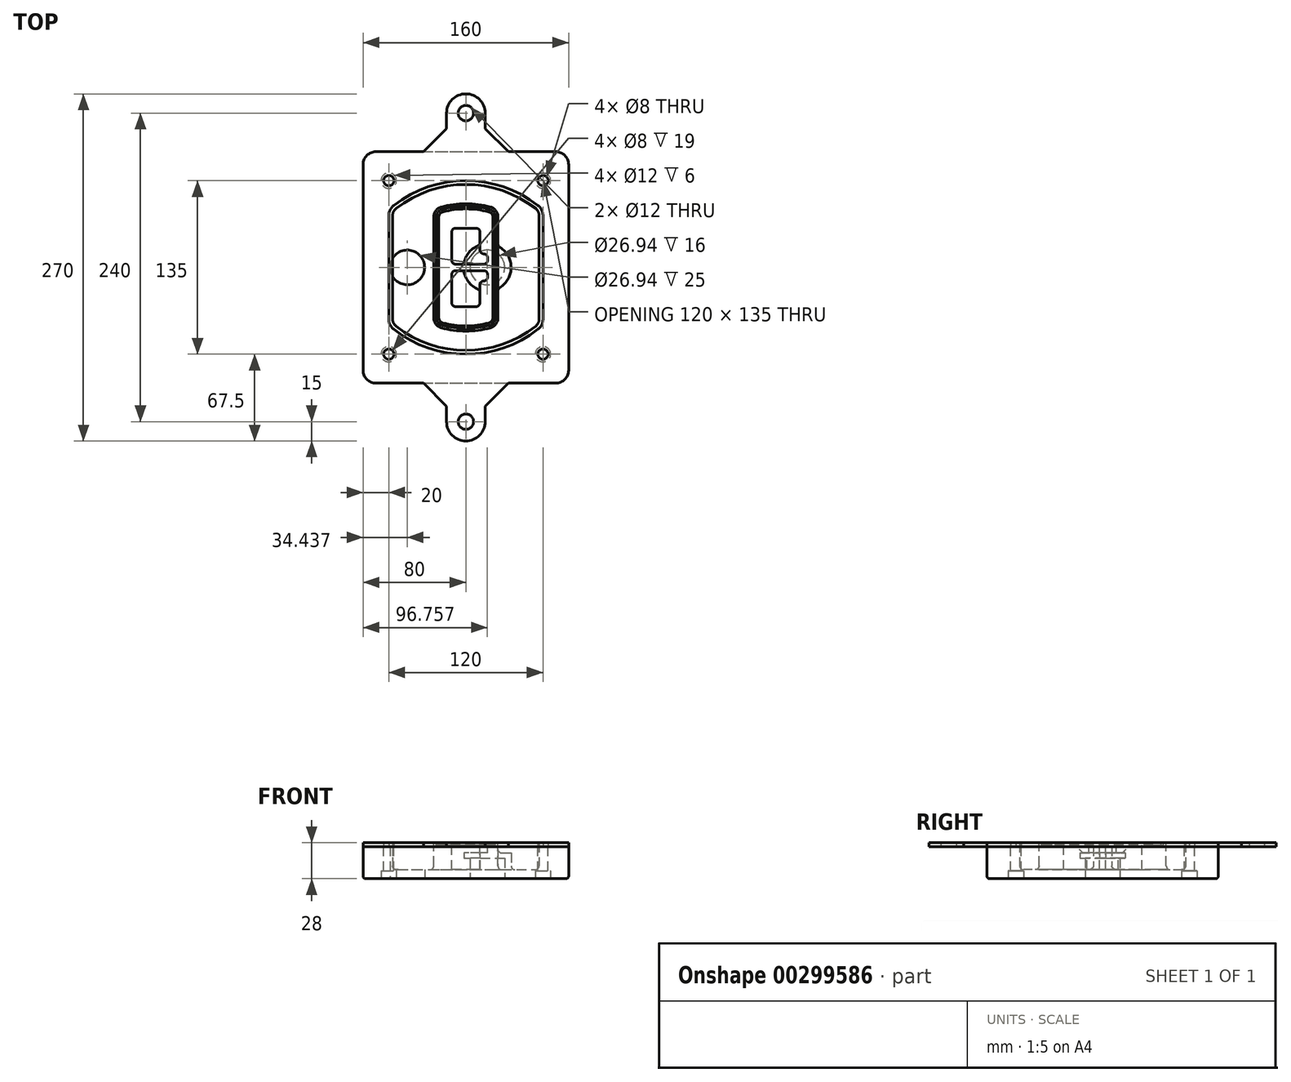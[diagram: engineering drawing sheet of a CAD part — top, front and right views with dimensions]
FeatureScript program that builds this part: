
annotation { "Feature Type Name" : "Feature", "Feature Type Description" : "" }
export const myFeature = defineFeature(function(context is Context, id is Id, definition is map)
    precondition{}
    {
        {
            var Q0;
            Q0=qCreatedBy(makeId("Top.planeOp"),FACE);
            var sketch = newSketch(context, id + "F0", { "sketchPlane" : qUnion([Q0])});
            skPoint(sketch, "E0.rect.middle", {"position": v(0, 0) * mm});
            skLineSegment(sketch, "E1.bottom", {"start": v(-70, -90) * mm, "end": v(70, -90) * mm});
            skLineSegment(sketch, "E1.top", {"start": v(-70, 90) * mm, "end": v(70, 90) * mm});
            skLineSegment(sketch, "E1.left", {"start": v(-80, -80) * mm, "end": v(-80, 80) * mm});
            skLineSegment(sketch, "E1.right", {"start": v(80, -80) * mm, "end": v(80, 80) * mm});
            skLineSegment(sketch, "E2", {"start": v(-80, 90) * mm, "end": v(80, -90) * mm, "construction": true});
            skLineSegment(sketch, "E3", {"start": v(80, 90) * mm, "end": v(-80, -90) * mm, "construction": true});
            skCircle(sketch, "E4", {"center": v(-60, 67.5) * mm, "radius": 4 * mm});
            skCircle(sketch, "E5", {"center": v(60, 67.5) * mm, "radius": 4 * mm});
            skCircle(sketch, "E6", {"center": v(60, -67.5) * mm, "radius": 4 * mm});
            skCircle(sketch, "E7", {"center": v(-60, -67.5) * mm, "radius": 4 * mm});
            skLineSegment(sketch, "E8", {"start": v(-60, 67.5) * mm, "end": v(60, 67.5) * mm, "construction": true});
            skLineSegment(sketch, "E9", {"start": v(60, 67.5) * mm, "end": v(60, -67.5) * mm, "construction": true});
            skLineSegment(sketch, "E10", {"start": v(60, -67.5) * mm, "end": v(-60, -67.5) * mm, "construction": true});
            skLineSegment(sketch, "E11", {"start": v(-60, -67.5) * mm, "end": v(-60, 67.5) * mm, "construction": true});
            skLineSegment(sketch, "E12", {"start": v(-60, 40.3) * mm, "end": v(-60, -40.3) * mm});
            skLineSegment(sketch, "E13", {"start": v(60, 40.3) * mm, "end": v(60, -40.3) * mm});
            skArc(sketch, "E14", {"start": v(56.15, 48.18) * mm, "mid": v(0, 67.5) * mm, "end": v(-56.15, 48.18) * mm});
            skArc(sketch, "E15", {"start": v(-56.15, -48.18) * mm, "mid": v(0, -67.5) * mm, "end": v(56.15, -48.18) * mm});
            skLineSegment(sketch, "E16", {"start": v(-60, 0) * mm, "end": v(60, 0) * mm, "construction": true});
            skPoint(sketch, "E17.visualSharp", {"position": v(-60, -45) * mm});
            skArc(sketch, "E17.filletArc", {"start": v(-60, -40.3) * mm, "mid": v(-58.99, -44.68) * mm, "end": v(-56.15, -48.18) * mm});
            skPoint(sketch, "E18.visualSharp", {"position": v(-60, 45) * mm});
            skArc(sketch, "E18.filletArc", {"start": v(-56.15, 48.18) * mm, "mid": v(-58.99, 44.68) * mm, "end": v(-60, 40.3) * mm});
            skPoint(sketch, "E19.visualSharp", {"position": v(60, 45) * mm});
            skArc(sketch, "E19.filletArc", {"start": v(60, 40.3) * mm, "mid": v(58.99, 44.68) * mm, "end": v(56.15, 48.18) * mm});
            skPoint(sketch, "E20.visualSharp", {"position": v(60, -45) * mm});
            skArc(sketch, "E20.filletArc", {"start": v(56.15, -48.18) * mm, "mid": v(58.99, -44.68) * mm, "end": v(60, -40.3) * mm});
            skPoint(sketch, "E21.visualSharp", {"position": v(-80, 90) * mm});
            skArc(sketch, "E21.filletArc", {"start": v(-70, 90) * mm, "mid": v(-77.07, 87.07) * mm, "end": v(-80, 80) * mm});
            skPoint(sketch, "E22.visualSharp", {"position": v(80, 90) * mm});
            skArc(sketch, "E22.filletArc", {"start": v(80, 80) * mm, "mid": v(77.07, 87.07) * mm, "end": v(70, 90) * mm});
            skPoint(sketch, "E23.visualSharp", {"position": v(80, -90) * mm});
            skArc(sketch, "E23.filletArc", {"start": v(70, -90) * mm, "mid": v(77.07, -87.07) * mm, "end": v(80, -80) * mm});
            skPoint(sketch, "E24.visualSharp", {"position": v(-80, -90) * mm});
            skArc(sketch, "E24.filletArc", {"start": v(-80, -80) * mm, "mid": v(-77.07, -87.07) * mm, "end": v(-70, -90) * mm});
            skArc(sketch, "E25.0", {"start": v(57, 40.3) * mm, "mid": v(56.3, 43.36) * mm, "end": v(54.3, 45.81) * mm});
            skLineSegment(sketch, "E25.1", {"start": v(57, 40.3) * mm, "end": v(57, -40.3) * mm});
            skArc(sketch, "E25.2", {"start": v(54.3, -45.81) * mm, "mid": v(56.3, -43.36) * mm, "end": v(57, -40.3) * mm});
            skArc(sketch, "E25.3", {"start": v(-54.3, -45.81) * mm, "mid": v(0, -64.5) * mm, "end": v(54.3, -45.81) * mm});
            skArc(sketch, "E25.4", {"start": v(-57, -40.3) * mm, "mid": v(-56.3, -43.36) * mm, "end": v(-54.3, -45.81) * mm});
            skArc(sketch, "E25.5", {"start": v(54.3, 45.81) * mm, "mid": v(0, 64.5) * mm, "end": v(-54.3, 45.81) * mm});
            skLineSegment(sketch, "E25.6", {"start": v(-57, 40.3) * mm, "end": v(-57, -40.3) * mm});
            skArc(sketch, "E25.7", {"start": v(-54.3, 45.81) * mm, "mid": v(-56.3, 43.36) * mm, "end": v(-57, 40.3) * mm});
            skArc(sketch, "E26.0", {"start": v(-58.62, 51.33) * mm, "mid": v(-62.58, 46.43) * mm, "end": v(-64, 40.3) * mm});
            skArc(sketch, "E26.1", {"start": v(58.62, 51.33) * mm, "mid": v(0, 71.5) * mm, "end": v(-58.62, 51.33) * mm});
            skArc(sketch, "E26.2", {"start": v(64, 40.3) * mm, "mid": v(62.58, 46.43) * mm, "end": v(58.62, 51.33) * mm});
            skLineSegment(sketch, "E26.3", {"start": v(64, 40.3) * mm, "end": v(64, -40.3) * mm});
            skArc(sketch, "E26.4", {"start": v(58.62, -51.33) * mm, "mid": v(62.58, -46.43) * mm, "end": v(64, -40.3) * mm});
            skLineSegment(sketch, "E26.5", {"start": v(-64, 40.3) * mm, "end": v(-64, -40.3) * mm});
            skArc(sketch, "E26.6", {"start": v(-58.62, -51.33) * mm, "mid": v(0, -71.5) * mm, "end": v(58.62, -51.33) * mm});
            skArc(sketch, "E26.7", {"start": v(-64, -40.3) * mm, "mid": v(-62.58, -46.43) * mm, "end": v(-58.62, -51.33) * mm});
            skSolve(sketch);
        }
        {
            var Q0;
            Q0=makeQuery(id+"F0.imprint","IMPRINT",FACE,{"disambiguationData":[TD([[makeQuery(id+"F0.imprint","IMPRINT",EDGE,{"derivedFrom":sQuery(id+"F0.wireOp",EDGE,"E1.bottom")}),1.0]])]});
            var Q1;
            Q1=makeQuery(id+"F0.imprint","IMPRINT",FACE,{"disambiguationData":[TD([[makeQuery(id+"F0.imprint","IMPRINT",EDGE,{"derivedFrom":sQuery(id+"F0.wireOp",EDGE,"E12")}),1.0]])]});
            var Q2;
            Q2=makeQuery(id+"F0.imprint","IMPRINT",FACE,{"disambiguationData":[TD([[makeQuery(id+"F0.imprint","IMPRINT",EDGE,{"derivedFrom":sQuery(id+"F0.wireOp",EDGE,"E25.0")}),1.0]])]});
            var Q3;
            Q3=makeQuery(id+"F0.imprint","IMPRINT",FACE,{"disambiguationData":[TD([[makeQuery(id+"F0.imprint","IMPRINT",EDGE,{"derivedFrom":sQuery(id+"F0.wireOp",EDGE,"E12")}),-1.0]])]});
            extrude(context, id + "F1", {"entities" : qUnion([Q0, Q1, Q2, Q3]), "oppositeDirection" : true, "depth" : 25 * mm});
        }
        {
            var Q0;
            Q0=makeQuery(id+"F0.imprint","IMPRINT",FACE,{"disambiguationData":[TD([[makeQuery(id+"F0.imprint","IMPRINT",EDGE,{"derivedFrom":sQuery(id+"F0.wireOp",EDGE,"E12")}),1.0]])]});
            extrude(context, id + "F2", {"entities" : qUnion([Q0]), "operationType" : NewBodyOperationType.ADD, "depth" : 3 * mm});
        }
        {
            var Q0;
            Q0=makeQuery(id+"F0.imprint","IMPRINT",FACE,{"disambiguationData":[TD([[makeQuery(id+"F0.imprint","IMPRINT",EDGE,{"derivedFrom":sQuery(id+"F0.wireOp",EDGE,"E25.0")}),1.0]])]});
            extrude(context, id + "F3", {"entities" : qUnion([Q0]), "operationType" : NewBodyOperationType.REMOVE, "oppositeDirection" : true, "depth" : 18 * mm});
        }
        {
            var Q0;
            Q0=makeQuery(id+"F2.opExtrude","CAP_FACE",FACE,{"disambiguationData":[OSD([sQuery(id+"F0.wireOp",EDGE,"E12"),sQuery(id+"F0.wireOp",EDGE,"E13"),sQuery(id+"F0.wireOp",EDGE,"E14"),sQuery(id+"F0.wireOp",EDGE,"E15"),sQuery(id+"F0.wireOp",EDGE,"E17.filletArc"),sQuery(id+"F0.wireOp",EDGE,"E18.filletArc"),sQuery(id+"F0.wireOp",EDGE,"E19.filletArc"),sQuery(id+"F0.wireOp",EDGE,"E20.filletArc"),sQuery(id+"F0.wireOp",EDGE,"E25.0"),sQuery(id+"F0.wireOp",EDGE,"E25.1"),sQuery(id+"F0.wireOp",EDGE,"E25.2"),sQuery(id+"F0.wireOp",EDGE,"E25.3"),sQuery(id+"F0.wireOp",EDGE,"E25.4"),sQuery(id+"F0.wireOp",EDGE,"E25.5"),sQuery(id+"F0.wireOp",EDGE,"E25.6"),sQuery(id+"F0.wireOp",EDGE,"E25.7")])],"isStart":false});
            var sketch = newSketch(context, id + "F4", { "sketchPlane" : qUnion([Q0])});
            skArc(sketch, "E27.0", {"start": v(-19.08, -46.97) * mm, "mid": v(0, -49.5) * mm, "end": v(19.08, -46.97) * mm});
            skArc(sketch, "E28.0", {"start": v(19.08, 46.97) * mm, "mid": v(0, 49.5) * mm, "end": v(-19.08, 46.97) * mm});
            skLineSegment(sketch, "E29", {"start": v(-25, 39.25) * mm, "end": v(-25, -39.25) * mm});
            skLineSegment(sketch, "E30", {"start": v(25, 39.25) * mm, "end": v(25, -39.25) * mm});
            skLineSegment(sketch, "E31", {"start": v(-25, 45.1) * mm, "end": v(25, 45.1) * mm, "construction": true});
            skLineSegment(sketch, "E32", {"start": v(-25, -45.1) * mm, "end": v(25, -45.1) * mm, "construction": true});
            skPoint(sketch, "E33.visualSharp", {"position": v(-25, 45.1) * mm});
            skArc(sketch, "E33.filletArc", {"start": v(-19.08, 46.97) * mm, "mid": v(-23.35, 44.11) * mm, "end": v(-25, 39.25) * mm});
            skPoint(sketch, "E34.visualSharp", {"position": v(25, 45.1) * mm});
            skArc(sketch, "E34.filletArc", {"start": v(25, 39.25) * mm, "mid": v(23.35, 44.11) * mm, "end": v(19.08, 46.97) * mm});
            skPoint(sketch, "E35.visualSharp", {"position": v(25, -45.1) * mm});
            skArc(sketch, "E35.filletArc", {"start": v(19.08, -46.97) * mm, "mid": v(23.35, -44.11) * mm, "end": v(25, -39.25) * mm});
            skPoint(sketch, "E36.visualSharp", {"position": v(-25, -45.1) * mm});
            skArc(sketch, "E36.filletArc", {"start": v(-25, -39.25) * mm, "mid": v(-23.35, -44.11) * mm, "end": v(-19.08, -46.97) * mm});
            skArc(sketch, "E37.0", {"start": v(54.3, 45.81) * mm, "mid": v(0, 64.5) * mm, "end": v(-54.3, 45.81) * mm});
            skArc(sketch, "E37.1", {"start": v(-54.3, 45.81) * mm, "mid": v(-56.3, 43.36) * mm, "end": v(-57, 40.3) * mm});
            skLineSegment(sketch, "E37.2", {"start": v(-57, 40.3) * mm, "end": v(-57, -40.3) * mm});
            skArc(sketch, "E37.3", {"start": v(-57, -40.3) * mm, "mid": v(-56.3, -43.36) * mm, "end": v(-54.3, -45.81) * mm});
            skArc(sketch, "E37.4", {"start": v(-54.3, -45.81) * mm, "mid": v(0, -64.5) * mm, "end": v(54.3, -45.81) * mm});
            skArc(sketch, "E37.5", {"start": v(54.3, -45.81) * mm, "mid": v(56.3, -43.36) * mm, "end": v(57, -40.3) * mm});
            skLineSegment(sketch, "E37.6", {"start": v(57, 40.3) * mm, "end": v(57, -40.3) * mm});
            skArc(sketch, "E37.7", {"start": v(57, 40.3) * mm, "mid": v(56.3, 43.36) * mm, "end": v(54.3, 45.81) * mm});
            skLineSegment(sketch, "E38.0", {"start": v(23, 39.25) * mm, "end": v(23, -39.25) * mm});
            skArc(sketch, "E38.1", {"start": v(18.56, -45.04) * mm, "mid": v(21.76, -42.9) * mm, "end": v(23, -39.25) * mm});
            skArc(sketch, "E38.2", {"start": v(-18.56, -45.04) * mm, "mid": v(0, -47.5) * mm, "end": v(18.56, -45.04) * mm});
            skArc(sketch, "E38.3", {"start": v(-23, -39.25) * mm, "mid": v(-21.76, -42.9) * mm, "end": v(-18.56, -45.04) * mm});
            skLineSegment(sketch, "E38.4", {"start": v(-23, 39.25) * mm, "end": v(-23, -39.25) * mm});
            skArc(sketch, "E38.5", {"start": v(23, 39.25) * mm, "mid": v(21.76, 42.9) * mm, "end": v(18.56, 45.04) * mm});
            skArc(sketch, "E38.6", {"start": v(-18.56, 45.04) * mm, "mid": v(-21.76, 42.9) * mm, "end": v(-23, 39.25) * mm});
            skArc(sketch, "E38.7", {"start": v(18.56, 45.04) * mm, "mid": v(0, 47.5) * mm, "end": v(-18.56, 45.04) * mm});
            skArc(sketch, "E39.0", {"start": v(21, 39.25) * mm, "mid": v(20.18, 41.68) * mm, "end": v(18.04, 43.1) * mm});
            skLineSegment(sketch, "E39.1", {"start": v(21, 39.25) * mm, "end": v(21, -39.25) * mm});
            skArc(sketch, "E39.2", {"start": v(18.04, -43.1) * mm, "mid": v(20.18, -41.68) * mm, "end": v(21, -39.25) * mm});
            skArc(sketch, "E39.3", {"start": v(-18.04, -43.1) * mm, "mid": v(0, -45.5) * mm, "end": v(18.04, -43.1) * mm});
            skArc(sketch, "E39.4", {"start": v(-21, -39.25) * mm, "mid": v(-20.18, -41.68) * mm, "end": v(-18.04, -43.1) * mm});
            skArc(sketch, "E39.5", {"start": v(18.04, 43.1) * mm, "mid": v(0, 45.5) * mm, "end": v(-18.04, 43.1) * mm});
            skLineSegment(sketch, "E39.6", {"start": v(-21, 39.25) * mm, "end": v(-21, -39.25) * mm});
            skArc(sketch, "E39.7", {"start": v(-18.04, 43.1) * mm, "mid": v(-20.18, 41.68) * mm, "end": v(-21, 39.25) * mm});
            skLineSegment(sketch, "E40", {"start": v(-25, 0) * mm, "end": v(25, 0) * mm, "construction": true});
            skLineSegment(sketch, "E41", {"start": v(-11, 5.5) * mm, "end": v(-11, 27.5) * mm});
            skLineSegment(sketch, "E42", {"start": v(-8, 30.5) * mm, "end": v(8, 30.5) * mm});
            skLineSegment(sketch, "E43", {"start": v(11, 27.5) * mm, "end": v(11, 13.5) * mm});
            skLineSegment(sketch, "E44", {"start": v(14, 10.5) * mm, "end": v(14, 10.5) * mm});
            skLineSegment(sketch, "E45", {"start": v(17, 7.5) * mm, "end": v(17, 5.5) * mm});
            skLineSegment(sketch, "E46", {"start": v(14, 2.5) * mm, "end": v(-8, 2.5) * mm});
            skPoint(sketch, "E47.visualSharp", {"position": v(-11, 30.5) * mm});
            skArc(sketch, "E47.filletArc", {"start": v(-8, 30.5) * mm, "mid": v(-10.12, 29.62) * mm, "end": v(-11, 27.5) * mm});
            skPoint(sketch, "E48.visualSharp", {"position": v(11, 30.5) * mm});
            skArc(sketch, "E48.filletArc", {"start": v(11, 27.5) * mm, "mid": v(10.12, 29.62) * mm, "end": v(8, 30.5) * mm});
            skPoint(sketch, "E49.visualSharp", {"position": v(11, 10.5) * mm});
            skArc(sketch, "E49.filletArc", {"start": v(11, 13.5) * mm, "mid": v(11.88, 11.38) * mm, "end": v(14, 10.5) * mm});
            skPoint(sketch, "E50.visualSharp", {"position": v(17, 10.5) * mm});
            skArc(sketch, "E50.filletArc", {"start": v(17, 7.5) * mm, "mid": v(16.12, 9.62) * mm, "end": v(14, 10.5) * mm});
            skPoint(sketch, "E51.visualSharp", {"position": v(17, 2.5) * mm});
            skArc(sketch, "E51.filletArc", {"start": v(14, 2.5) * mm, "mid": v(16.12, 3.38) * mm, "end": v(17, 5.5) * mm});
            skPoint(sketch, "E52.visualSharp", {"position": v(-11, 2.5) * mm});
            skArc(sketch, "E52.filletArc", {"start": v(-11, 5.5) * mm, "mid": v(-10.12, 3.38) * mm, "end": v(-8, 2.5) * mm});
            skLineSegment(sketch, "E53.0.MirrorCS", {"start": v(14, -2.5) * mm, "end": v(-8, -2.5) * mm});
            skArc(sketch, "E54.0.MirrorCS", {"start": v(-11, -5.5) * mm, "mid": v(-10.12, -3.38) * mm, "end": v(-8, -2.5) * mm});
            skLineSegment(sketch, "E55.0.MirrorCS", {"start": v(-11, -5.5) * mm, "end": v(-11, -27.5) * mm});
            skArc(sketch, "E56.0.MirrorCS", {"start": v(-8, -30.5) * mm, "mid": v(-10.12, -29.62) * mm, "end": v(-11, -27.5) * mm});
            skLineSegment(sketch, "E57.0.MirrorCS", {"start": v(-8, -30.5) * mm, "end": v(8, -30.5) * mm});
            skArc(sketch, "E58.0.MirrorCS", {"start": v(11, -27.5) * mm, "mid": v(10.12, -29.62) * mm, "end": v(8, -30.5) * mm});
            skLineSegment(sketch, "E59.0.MirrorCS", {"start": v(11, -27.5) * mm, "end": v(11, -13.5) * mm});
            skArc(sketch, "E60.0.MirrorCS", {"start": v(11, -13.5) * mm, "mid": v(11.88, -11.38) * mm, "end": v(14, -10.5) * mm});
            skArc(sketch, "E61.0.MirrorCS", {"start": v(17, -7.5) * mm, "mid": v(16.12, -9.62) * mm, "end": v(14, -10.5) * mm});
            skLineSegment(sketch, "E62.0.MirrorCS", {"start": v(17, -7.5) * mm, "end": v(17, -5.5) * mm});
            skArc(sketch, "E63.0.MirrorCS", {"start": v(14, -2.5) * mm, "mid": v(16.12, -3.38) * mm, "end": v(17, -5.5) * mm});
            skSolve(sketch);
        }
        {
            var Q0;
            Q0=makeQuery(id+"F4.imprint","IMPRINT",FACE,{"disambiguationData":[TD([[makeQuery(id+"F4.imprint","IMPRINT",EDGE,{"derivedFrom":sQuery(id+"F4.wireOp",EDGE,"E27.0")}),1.0]])]});
            var Q1;
            Q1=makeQuery(id+"F4.imprint","IMPRINT",FACE,{"disambiguationData":[TD([[makeQuery(id+"F4.imprint","IMPRINT",EDGE,{"derivedFrom":sQuery(id+"F4.wireOp",EDGE,"E38.0")}),-1.0]])]});
            var Q2;
            Q2=makeQuery(id+"F4.imprint","IMPRINT",FACE,{"disambiguationData":[TD([[makeQuery(id+"F4.imprint","IMPRINT",EDGE,{"derivedFrom":sQuery(id+"F4.wireOp",EDGE,"E39.0")}),1.0]])]});
            extrude(context, id + "F5", {"entities" : qUnion([Q0, Q1, Q2]), "operationType" : NewBodyOperationType.ADD, "endBound" : BoundingType.UP_TO_NEXT, "oppositeDirection" : true, "depth" : 25 * mm});
        }
        {
            var Q0;
            Q0=makeQuery(id+"F4.imprint","IMPRINT",FACE,{"disambiguationData":[TD([[makeQuery(id+"F4.imprint","IMPRINT",EDGE,{"derivedFrom":sQuery(id+"F4.wireOp",EDGE,"E38.0")}),-1.0]])]});
            extrude(context, id + "F6", {"entities" : qUnion([Q0]), "operationType" : NewBodyOperationType.REMOVE, "oppositeDirection" : true, "depth" : 2 * mm});
        }
        {
            var Q0;
            Q0=makeQuery(id+"F1.opExtrude","CAP_FACE",FACE,{"disambiguationData":[OSD([sQuery(id+"F0.wireOp",EDGE,"E1.bottom"),sQuery(id+"F0.wireOp",EDGE,"E1.top"),sQuery(id+"F0.wireOp",EDGE,"E1.left"),sQuery(id+"F0.wireOp",EDGE,"E1.right"),sQuery(id+"F0.wireOp",EDGE,"E4"),sQuery(id+"F0.wireOp",EDGE,"E5"),sQuery(id+"F0.wireOp",EDGE,"E6"),sQuery(id+"F0.wireOp",EDGE,"E7"),sQuery(id+"F0.wireOp",EDGE,"E21.filletArc"),sQuery(id+"F0.wireOp",EDGE,"E22.filletArc"),sQuery(id+"F0.wireOp",EDGE,"E23.filletArc"),sQuery(id+"F0.wireOp",EDGE,"E24.filletArc")])],"isStart":false});
            var sketch = newSketch(context, id + "F7", { "sketchPlane" : qUnion([Q0])});
            skCircle(sketch, "E64", {"center": v(16.76, 0) * mm, "radius": 13.47 * mm});
            skCircle(sketch, "E65", {"center": v(-45.56, 0) * mm, "radius": 13.47 * mm});
            skLineSegment(sketch, "E66", {"start": v(80, 0) * mm, "end": v(-80, 0) * mm});
            skCircle(sketch, "E67", {"center": v(16.76, 0) * mm, "radius": 18.47 * mm});
            skCircle(sketch, "E68", {"center": v(60, -67.5) * mm, "radius": 6 * mm});
            skCircle(sketch, "E69", {"center": v(-60, -67.5) * mm, "radius": 6 * mm});
            skCircle(sketch, "E70", {"center": v(-60, 67.5) * mm, "radius": 6 * mm});
            skCircle(sketch, "E71", {"center": v(60, 67.5) * mm, "radius": 6 * mm});
            skSolve(sketch);
        }
        {
            var Q0;
            {var subQ1=sQuery(id+"F7.wireOp",EDGE,"E66");var subQ4=sQuery(id+"F7.wireOp",EDGE,"E64");var subQ6=makeQuery(id+"F7.imprint","INTERSECT",VERTEX,{"disambiguationData":[OD(0.0)],"derivedFrom":[subQ4,subQ1]});Q0=makeQuery(id+"F7.imprint","IMPRINT",FACE,{"disambiguationData":[TD([[makeQuery(id+"F7.imprint","IMPRINT",EDGE,{"disambiguationData":[TD([[subQ6,-1.0]])],"derivedFrom":subQ4}),-1.0]])]});}
            var Q1;
            {var subQ0=sQuery(id+"F7.wireOp",EDGE,"E66");var subQ1=sQuery(id+"F7.wireOp",EDGE,"E64");var subQ3=makeQuery(id+"F7.imprint","INTERSECT",VERTEX,{"disambiguationData":[OD(0.0)],"derivedFrom":[subQ1,subQ0]});Q1=makeQuery(id+"F7.imprint","IMPRINT",FACE,{"disambiguationData":[TD([[makeQuery(id+"F7.imprint","IMPRINT",EDGE,{"disambiguationData":[TD([[subQ3,-1.0]])],"derivedFrom":subQ1}),1.0]])]});}
            var Q2;
            {var subQ0=sQuery(id+"F7.wireOp",EDGE,"E66");var subQ1=sQuery(id+"F7.wireOp",EDGE,"E64");var subQ3=makeQuery(id+"F7.imprint","INTERSECT",VERTEX,{"disambiguationData":[OD(0.0)],"derivedFrom":[subQ1,subQ0]});Q2=makeQuery(id+"F7.imprint","IMPRINT",FACE,{"disambiguationData":[TD([[makeQuery(id+"F7.imprint","IMPRINT",EDGE,{"disambiguationData":[TD([[subQ3,1.0]])],"derivedFrom":subQ1}),1.0]])]});}
            var Q3;
            {var subQ1=sQuery(id+"F7.wireOp",EDGE,"E66");var subQ4=sQuery(id+"F7.wireOp",EDGE,"E64");var subQ6=makeQuery(id+"F7.imprint","INTERSECT",VERTEX,{"disambiguationData":[OD(0.0)],"derivedFrom":[subQ4,subQ1]});Q3=makeQuery(id+"F7.imprint","IMPRINT",FACE,{"disambiguationData":[TD([[makeQuery(id+"F7.imprint","IMPRINT",EDGE,{"disambiguationData":[TD([[subQ6,1.0]])],"derivedFrom":subQ4}),-1.0]])]});}
            extrude(context, id + "F8", {"entities" : qUnion([Q0, Q1, Q2, Q3]), "operationType" : NewBodyOperationType.ADD, "oppositeDirection" : true, "depth" : 20 * mm});
        }
        {
            var Q0;
            {var subQ0=sQuery(id+"F7.wireOp",EDGE,"E66");var subQ1=sQuery(id+"F7.wireOp",EDGE,"E64");var subQ3=makeQuery(id+"F7.imprint","INTERSECT",VERTEX,{"disambiguationData":[OD(0.0)],"derivedFrom":[subQ1,subQ0]});Q0=makeQuery(id+"F7.imprint","IMPRINT",FACE,{"disambiguationData":[TD([[makeQuery(id+"F7.imprint","IMPRINT",EDGE,{"disambiguationData":[TD([[subQ3,-1.0]])],"derivedFrom":subQ1}),1.0]])]});}
            var Q1;
            {var subQ0=sQuery(id+"F7.wireOp",EDGE,"E66");var subQ1=sQuery(id+"F7.wireOp",EDGE,"E64");var subQ3=makeQuery(id+"F7.imprint","INTERSECT",VERTEX,{"disambiguationData":[OD(0.0)],"derivedFrom":[subQ1,subQ0]});Q1=makeQuery(id+"F7.imprint","IMPRINT",FACE,{"disambiguationData":[TD([[makeQuery(id+"F7.imprint","IMPRINT",EDGE,{"disambiguationData":[TD([[subQ3,1.0]])],"derivedFrom":subQ1}),1.0]])]});}
            extrude(context, id + "F9", {"entities" : qUnion([Q0, Q1]), "operationType" : NewBodyOperationType.REMOVE, "oppositeDirection" : true, "depth" : 16 * mm});
        }
        {
            var Q0;
            {var subQ0=sQuery(id+"F7.wireOp",EDGE,"E66");var subQ1=sQuery(id+"F7.wireOp",EDGE,"E65");var subQ3=makeQuery(id+"F7.imprint","INTERSECT",VERTEX,{"disambiguationData":[OD(0.0)],"derivedFrom":[subQ1,subQ0]});Q0=makeQuery(id+"F7.imprint","IMPRINT",FACE,{"disambiguationData":[TD([[makeQuery(id+"F7.imprint","IMPRINT",EDGE,{"disambiguationData":[TD([[subQ3,-1.0]])],"derivedFrom":subQ1}),1.0]])]});}
            var Q1;
            {var subQ0=sQuery(id+"F7.wireOp",EDGE,"E66");var subQ1=sQuery(id+"F7.wireOp",EDGE,"E65");var subQ3=makeQuery(id+"F7.imprint","INTERSECT",VERTEX,{"disambiguationData":[OD(0.0)],"derivedFrom":[subQ1,subQ0]});Q1=makeQuery(id+"F7.imprint","IMPRINT",FACE,{"disambiguationData":[TD([[makeQuery(id+"F7.imprint","IMPRINT",EDGE,{"disambiguationData":[TD([[subQ3,1.0]])],"derivedFrom":subQ1}),1.0]])]});}
            extrude(context, id + "F10", {"entities" : qUnion([Q0, Q1]), "operationType" : NewBodyOperationType.REMOVE, "oppositeDirection" : true, "depth" : 25 * mm});
        }
        {
            var Q0;
            Q0=makeQuery(id+"F7.imprint","IMPRINT",FACE,{"disambiguationData":[TD([[makeQuery(id+"F7.imprint","IMPRINT",EDGE,{"derivedFrom":sQuery(id+"F7.wireOp",EDGE,"E68")}),1.0]])]});
            var Q1;
            Q1=makeQuery(id+"F7.imprint","IMPRINT",FACE,{"disambiguationData":[TD([[makeQuery(id+"F7.imprint","IMPRINT",EDGE,{"derivedFrom":makeQuery(id+"F1.opExtrude","CAP_EDGE",EDGE,{"disambiguationData":[OSD([sQuery(id+"F0.wireOp",EDGE,"E5")])],"isStart":false})}),-1.0]])]});
            var Q2;
            Q2=makeQuery(id+"F7.imprint","IMPRINT",FACE,{"disambiguationData":[TD([[makeQuery(id+"F7.imprint","IMPRINT",EDGE,{"derivedFrom":sQuery(id+"F7.wireOp",EDGE,"E69")}),1.0]])]});
            var Q3;
            Q3=makeQuery(id+"F7.imprint","IMPRINT",FACE,{"disambiguationData":[TD([[makeQuery(id+"F7.imprint","IMPRINT",EDGE,{"derivedFrom":makeQuery(id+"F1.opExtrude","CAP_EDGE",EDGE,{"disambiguationData":[OSD([sQuery(id+"F0.wireOp",EDGE,"E4")])],"isStart":false})}),-1.0]])]});
            var Q4;
            Q4=makeQuery(id+"F7.imprint","IMPRINT",FACE,{"disambiguationData":[TD([[makeQuery(id+"F7.imprint","IMPRINT",EDGE,{"derivedFrom":sQuery(id+"F7.wireOp",EDGE,"E70")}),1.0]])]});
            var Q5;
            Q5=makeQuery(id+"F7.imprint","IMPRINT",FACE,{"disambiguationData":[TD([[makeQuery(id+"F7.imprint","IMPRINT",EDGE,{"derivedFrom":makeQuery(id+"F1.opExtrude","CAP_EDGE",EDGE,{"disambiguationData":[OSD([sQuery(id+"F0.wireOp",EDGE,"E7")])],"isStart":false})}),-1.0]])]});
            var Q6;
            Q6=makeQuery(id+"F7.imprint","IMPRINT",FACE,{"disambiguationData":[TD([[makeQuery(id+"F7.imprint","IMPRINT",EDGE,{"derivedFrom":sQuery(id+"F7.wireOp",EDGE,"E71")}),1.0]])]});
            var Q7;
            Q7=makeQuery(id+"F7.imprint","IMPRINT",FACE,{"disambiguationData":[TD([[makeQuery(id+"F7.imprint","IMPRINT",EDGE,{"derivedFrom":makeQuery(id+"F1.opExtrude","CAP_EDGE",EDGE,{"disambiguationData":[OSD([sQuery(id+"F0.wireOp",EDGE,"E6")])],"isStart":false})}),-1.0]])]});
            extrude(context, id + "F11", {"entities" : qUnion([Q0, Q1, Q2, Q3, Q4, Q5, Q6, Q7]), "operationType" : NewBodyOperationType.REMOVE, "oppositeDirection" : true, "depth" : 6 * mm});
        }
        {
            var Q0;
            Q0=makeQuery(id+"F9.boolean.opBoolean","COPY",FACE,{"derivedFrom":makeQuery(id+"F9.opExtrude","CAP_FACE",FACE,{"disambiguationData":[OSD([sQuery(id+"F7.wireOp",EDGE,"E64")])],"isStart":false})});
            var sketch = newSketch(context, id + "F12", { "sketchPlane" : qUnion([Q0])});
            skArc(sketch, "E72.0", {"start": v(11, 17.55) * mm, "mid": v(2.57, 11.82) * mm, "end": v(-1.54, 2.5) * mm});
            skArc(sketch, "E72.1", {"start": v(-1.54, -2.5) * mm, "mid": v(2.57, -11.82) * mm, "end": v(11, -17.55) * mm});
            skLineSegment(sketch, "E73", {"start": v(-1.54, -2.5) * mm, "end": v(14, -2.5) * mm});
            skLineSegment(sketch, "E74.0", {"start": v(14, 2.5) * mm, "end": v(-1.54, 2.5) * mm});
            skArc(sketch, "E74.1", {"start": v(14, 2.5) * mm, "mid": v(16.12, 3.38) * mm, "end": v(17, 5.5) * mm});
            skLineSegment(sketch, "E74.2", {"start": v(17, 7.5) * mm, "end": v(17, 5.5) * mm});
            skArc(sketch, "E74.3", {"start": v(17, 7.5) * mm, "mid": v(16.12, 9.62) * mm, "end": v(14, 10.5) * mm});
            skArc(sketch, "E74.4", {"start": v(11, 13.5) * mm, "mid": v(11.88, 11.38) * mm, "end": v(14, 10.5) * mm});
            skLineSegment(sketch, "E74.5", {"start": v(11, 17.55) * mm, "end": v(11, 13.5) * mm});
            skLineSegment(sketch, "E74.7", {"start": v(14, -2.5) * mm, "end": v(-1.54, -2.5) * mm});
            skArc(sketch, "E74.8", {"start": v(14, -2.5) * mm, "mid": v(16.12, -3.38) * mm, "end": v(17, -5.5) * mm});
            skLineSegment(sketch, "E74.9", {"start": v(17, -7.5) * mm, "end": v(17, -5.5) * mm});
            skArc(sketch, "E74.10", {"start": v(17, -7.5) * mm, "mid": v(16.12, -9.62) * mm, "end": v(14, -10.5) * mm});
            skArc(sketch, "E74.11", {"start": v(11, -13.5) * mm, "mid": v(11.88, -11.38) * mm, "end": v(14, -10.5) * mm});
            skLineSegment(sketch, "E74.12", {"start": v(11, -17.55) * mm, "end": v(11, -13.5) * mm});
            skPoint(sketch, "E75.orphan", {"position": v(11, -27.5) * mm});
            skPoint(sketch, "E76.orphan", {"position": v(-8, -2.5) * mm});
            skPoint(sketch, "E77.orphan", {"position": v(-8, 2.5) * mm});
            skPoint(sketch, "E78.orphan", {"position": v(11, 27.5) * mm});
            skSolve(sketch);
        }
        {
            var Q0;
            {var subQ7=sQuery(id+"F12.wireOp",EDGE,"E72.0");var subQ14=sQuery(id+"F12.wireOp",EDGE,"E72.1");var subQ16=sQuery(id+"F12.wireOp",EDGE,"E74.1");var subQ18=sQuery(id+"F12.wireOp",EDGE,"E74.8");Q0=qUnion([makeQuery(id+"F12.imprint","IMPRINT",FACE,{"disambiguationData":[TD([[makeQuery(id+"F12.imprint","IMPRINT",EDGE,{"derivedFrom":subQ7}),1.0]])]}),makeQuery(id+"F12.imprint","IMPRINT",FACE,{"disambiguationData":[TD([[makeQuery(id+"F12.imprint","IMPRINT",EDGE,{"derivedFrom":subQ14}),1.0]])]}),makeQuery(id+"F12.imprint","IMPRINT",FACE,{"disambiguationData":[TD([[makeQuery(id+"F12.imprint","IMPRINT",EDGE,{"derivedFrom":subQ16}),1.0]])]}),makeQuery(id+"F12.imprint","IMPRINT",FACE,{"disambiguationData":[TD([[makeQuery(id+"F12.imprint","IMPRINT",EDGE,{"derivedFrom":subQ18}),-1.0]])]})]);}
            var Q1;
            Q1=makeQuery(id+"F5.boolean.opBoolean","SPLIT",FACE,{"disambiguationData":[TD([makeQuery(id+"F5.opExtrude","SWEPT_FACE",FACE,{"disambiguationData":[OSD([sQuery(id+"F4.wireOp",EDGE,"E41")])]})])],"derivedFrom":makeQuery(id+"F3.boolean.opBoolean","COPY",FACE,{"derivedFrom":makeQuery(id+"F3.opExtrude","CAP_FACE",FACE,{"disambiguationData":[OSD([sQuery(id+"F0.wireOp",EDGE,"E25.0"),sQuery(id+"F0.wireOp",EDGE,"E25.1"),sQuery(id+"F0.wireOp",EDGE,"E25.2"),sQuery(id+"F0.wireOp",EDGE,"E25.3"),sQuery(id+"F0.wireOp",EDGE,"E25.4"),sQuery(id+"F0.wireOp",EDGE,"E25.5"),sQuery(id+"F0.wireOp",EDGE,"E25.6"),sQuery(id+"F0.wireOp",EDGE,"E25.7")])],"isStart":false})})});
            extrude(context, id + "F13", {"entities" : qUnion([Q0]), "operationType" : NewBodyOperationType.REMOVE, "endBound" : BoundingType.UP_TO_SURFACE, "endBoundEntityFace" : qUnion([Q1]), "depth" : 25 * mm});
        }
        {
            var Q0;
            Q0=makeQuery(id+"F3.boolean.opBoolean","COPY",EDGE,{"derivedFrom":makeQuery(id+"F3.opExtrude","CAP_EDGE",EDGE,{"disambiguationData":[OSD([sQuery(id+"F0.wireOp",EDGE,"E25.6")])],"isStart":false})});
            var Q1;
            Q1=makeQuery(id+"F8.boolean.opBoolean","INTERSECT",EDGE,{"derivedFrom":[makeQuery(id+"F5.opExtrude","SWEPT_FACE",FACE,{"disambiguationData":[OSD([sQuery(id+"F4.wireOp",EDGE,"E30")])]}),makeQuery(id+"F8.opExtrude","CAP_FACE",FACE,{"disambiguationData":[OSD([sQuery(id+"F7.wireOp",EDGE,"E67")])],"isStart":false})]});
            var Q2;
            Q2=makeQuery(id+"F8.boolean.opBoolean","INTERSECT",EDGE,{"disambiguationData":[OD(1.0)],"derivedFrom":[makeQuery(id+"F5.opExtrude","SWEPT_FACE",FACE,{"disambiguationData":[OSD([sQuery(id+"F4.wireOp",EDGE,"E30")])]}),makeQuery(id+"F8.opExtrude","SWEPT_FACE",FACE,{"disambiguationData":[OSD([sQuery(id+"F7.wireOp",EDGE,"E67")])]})]});
            var Q3;
            {var subQ0=sQuery(id+"F4.wireOp",EDGE,"E30");Q3=makeQuery(id+"F8.boolean.opBoolean","SPLIT",EDGE,{"disambiguationData":[TD([makeQuery(id+"F5.opExtrude","SWEPT_FACE",FACE,{"disambiguationData":[OSD([sQuery(id+"F4.wireOp",EDGE,"E35.filletArc")])]})])],"derivedFrom":makeQuery(id+"F5.opExtrude","CAP_EDGE",EDGE,{"disambiguationData":[OSD([subQ0])],"isStart":false})});}
            var Q4;
            {var subQ0=sQuery(id+"F0.wireOp",EDGE,"E25.7");var subQ1=sQuery(id+"F0.wireOp",EDGE,"E25.1");var subQ2=sQuery(id+"F0.wireOp",EDGE,"E25.6");var subQ3=sQuery(id+"F0.wireOp",EDGE,"E25.5");var subQ4=sQuery(id+"F0.wireOp",EDGE,"E25.4");var subQ5=sQuery(id+"F0.wireOp",EDGE,"E25.0");var subQ6=sQuery(id+"F0.wireOp",EDGE,"E25.2");var subQ7=sQuery(id+"F0.wireOp",EDGE,"E25.3");Q4=makeQuery(id+"F8.boolean.opBoolean","INTERSECT",EDGE,{"derivedFrom":[makeQuery(id+"F5.boolean.opBoolean","SPLIT",FACE,{"disambiguationData":[TD([makeQuery(id+"F2.opExtrude","SWEPT_FACE",FACE,{"disambiguationData":[OSD([subQ5])]})])],"derivedFrom":makeQuery(id+"F3.boolean.opBoolean","COPY",FACE,{"derivedFrom":makeQuery(id+"F3.opExtrude","CAP_FACE",FACE,{"disambiguationData":[OSD([subQ5,subQ1,subQ6,subQ7,subQ4,subQ3,subQ2,subQ0])],"isStart":false})})}),makeQuery(id+"F8.opExtrude","SWEPT_FACE",FACE,{"disambiguationData":[OSD([sQuery(id+"F7.wireOp",EDGE,"E67")])]})]});}
            var Q5;
            Q5=makeQuery(id+"F8.boolean.opBoolean","INTERSECT",EDGE,{"disambiguationData":[OD(0.0)],"derivedFrom":[makeQuery(id+"F5.opExtrude","SWEPT_FACE",FACE,{"disambiguationData":[OSD([sQuery(id+"F4.wireOp",EDGE,"E30")])]}),makeQuery(id+"F8.opExtrude","SWEPT_FACE",FACE,{"disambiguationData":[OSD([sQuery(id+"F7.wireOp",EDGE,"E67")])]})]});
            fillet(context, id + "F14", {"entities" : qUnion([Q0, Q1, Q2, Q3, Q4, Q5]), "radius" : 3 * mm, "tangentPropagation" : true, "allowEdgeOverflow" : false});
        }
        {
            var Q0;
            Q0=makeQuery(id+"F1.opExtrude","CAP_EDGE",EDGE,{"disambiguationData":[OSD([sQuery(id+"F0.wireOp",EDGE,"E1.bottom")])],"isStart":false});
            fillet(context, id + "F15", {"entities" : qUnion([Q0]), "radius" : 2 * mm, "tangentPropagation" : true, "allowEdgeOverflow" : false});
        }
        {
            var Q0;
            {var subQ0=sQuery(id+"F0.wireOp",EDGE,"E21.filletArc");var subQ1=sQuery(id+"F0.wireOp",EDGE,"E7");var subQ2=sQuery(id+"F0.wireOp",EDGE,"E6");var subQ3=sQuery(id+"F0.wireOp",EDGE,"E5");var subQ4=sQuery(id+"F0.wireOp",EDGE,"E4");var subQ5=sQuery(id+"F0.wireOp",EDGE,"E22.filletArc");var subQ6=sQuery(id+"F0.wireOp",EDGE,"E1.bottom");var subQ7=sQuery(id+"F0.wireOp",EDGE,"E1.right");var subQ8=sQuery(id+"F0.wireOp",EDGE,"E1.top");var subQ9=sQuery(id+"F0.wireOp",EDGE,"E1.left");var subQ10=sQuery(id+"F0.wireOp",EDGE,"E23.filletArc");var subQ11=sQuery(id+"F0.wireOp",EDGE,"E24.filletArc");Q0=makeQuery(id+"F2.boolean.opBoolean","SPLIT",FACE,{"disambiguationData":[TD([makeQuery(id+"F1.opExtrude","SWEPT_FACE",FACE,{"disambiguationData":[OSD([subQ6])]})])],"derivedFrom":makeQuery(id+"F1.opExtrude","CAP_FACE",FACE,{"disambiguationData":[OSD([subQ6,subQ8,subQ9,subQ7,subQ4,subQ3,subQ2,subQ1,subQ0,subQ5,subQ10,subQ11])],"isStart":true})});}
            var sketch = newSketch(context, id + "F16", { "sketchPlane" : qUnion([Q0])});
            skLineSegment(sketch, "E79", {"start": v(0, 90) * mm, "end": v(0, 120) * mm, "construction": true});
            skCircle(sketch, "E80", {"center": v(0, 120) * mm, "radius": 6 * mm});
            skArc(sketch, "E81", {"start": v(15, 120) * mm, "mid": v(0, 135) * mm, "end": v(-15, 120) * mm});
            skLineSegment(sketch, "E82", {"start": v(-15, 120) * mm, "end": v(-15, 108) * mm});
            skLineSegment(sketch, "E83", {"start": v(15, 120) * mm, "end": v(15, 108) * mm});
            skLineSegment(sketch, "E84", {"start": v(-15, 108) * mm, "end": v(-33, 90) * mm});
            skLineSegment(sketch, "E85", {"start": v(15, 108) * mm, "end": v(33, 90) * mm});
            skLineSegment(sketch, "E86", {"start": v(0, -90) * mm, "end": v(0, -120) * mm, "construction": true});
            skCircle(sketch, "E87", {"center": v(0, -120) * mm, "radius": 6 * mm});
            skArc(sketch, "E88", {"start": v(-15, -120) * mm, "mid": v(0, -135) * mm, "end": v(15, -120) * mm});
            skLineSegment(sketch, "E89", {"start": v(15, -120) * mm, "end": v(15, -108) * mm});
            skLineSegment(sketch, "E90", {"start": v(-15, -120) * mm, "end": v(-15, -108) * mm});
            skLineSegment(sketch, "E91", {"start": v(15, -108) * mm, "end": v(33, -90) * mm});
            skLineSegment(sketch, "E92", {"start": v(-15, -108) * mm, "end": v(-33, -90) * mm});
            skSolve(sketch);
        }
        {
            var Q0;
            Q0=makeQuery(id+"F16.imprint","IMPRINT",FACE,{"disambiguationData":[TD([[makeQuery(id+"F16.imprint","IMPRINT",EDGE,{"derivedFrom":sQuery(id+"F16.wireOp",EDGE,"E80")}),-1.0]])]});
            var Q1;
            Q1=makeQuery(id+"F16.imprint","IMPRINT",FACE,{"disambiguationData":[TD([[makeQuery(id+"F16.imprint","IMPRINT",EDGE,{"derivedFrom":sQuery(id+"F16.wireOp",EDGE,"E87")}),-1.0]])]});
            var Q2;
            Q2=makeQuery(id+"F16.imprint","IMPRINT",FACE,{"disambiguationData":[TD([[makeQuery(id+"F16.imprint","IMPRINT",EDGE,{"derivedFrom":makeQuery(id+"F1.opExtrude","CAP_EDGE",EDGE,{"disambiguationData":[OSD([sQuery(id+"F0.wireOp",EDGE,"E1.left")])],"isStart":true})}),-1.0]])]});
            var Q3;
            Q3=makeQuery(id+"F2.opExtrude","CAP_FACE",FACE,{"disambiguationData":[OSD([sQuery(id+"F0.wireOp",EDGE,"E12"),sQuery(id+"F0.wireOp",EDGE,"E13"),sQuery(id+"F0.wireOp",EDGE,"E14"),sQuery(id+"F0.wireOp",EDGE,"E15"),sQuery(id+"F0.wireOp",EDGE,"E17.filletArc"),sQuery(id+"F0.wireOp",EDGE,"E18.filletArc"),sQuery(id+"F0.wireOp",EDGE,"E19.filletArc"),sQuery(id+"F0.wireOp",EDGE,"E20.filletArc"),sQuery(id+"F0.wireOp",EDGE,"E25.0"),sQuery(id+"F0.wireOp",EDGE,"E25.1"),sQuery(id+"F0.wireOp",EDGE,"E25.2"),sQuery(id+"F0.wireOp",EDGE,"E25.3"),sQuery(id+"F0.wireOp",EDGE,"E25.4"),sQuery(id+"F0.wireOp",EDGE,"E25.5"),sQuery(id+"F0.wireOp",EDGE,"E25.6"),sQuery(id+"F0.wireOp",EDGE,"E25.7")])],"isStart":false});
            extrude(context, id + "F17", {"entities" : qUnion([Q0, Q1, Q2]), "endBound" : BoundingType.UP_TO_SURFACE, "endBoundEntityFace" : qUnion([Q3]), "depth" : 25 * mm});
        }
    });
